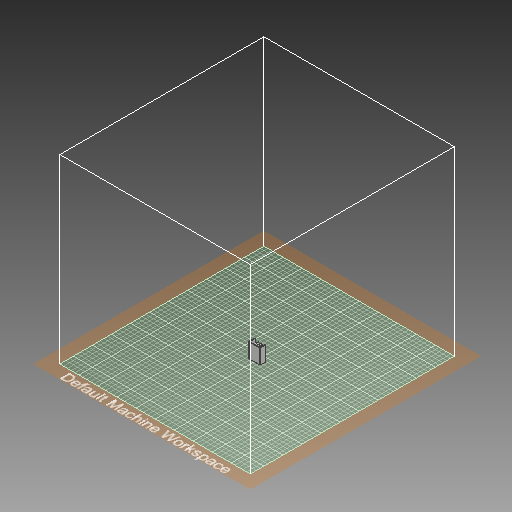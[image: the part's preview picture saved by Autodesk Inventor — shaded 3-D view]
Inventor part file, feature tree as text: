
AUTODESK INVENTOR PART (.ipt)
format: ipt  version: 2019.3 (Build 233278000, 278)  size: 1,133,056 bytes
history: native  units: mm
features: extrude x4, sketch x4, other x3, mirror x1, projected_geometry x1
ambient origin geometry x8: Origin, YZ Plane, XZ Plane, XY Plane, X Axis, Y Axis, Z Axis, Center Point
bodies: Body1 (feature_tree)
feature tree (13):
  extrude  "Extrusion2"  Depth=0.5mm
  extrude  "Extrusion4"  Depth=0.5mm
  mirror  "Mirror1"
  extrude  "Extrusion5"  Depth=0.5mm
  extrude  "Extrusion6"  Depth=1.0mm TaperAngle=360.0deg
  sketch  "Sketch5"  dims[d9=30.0deg d10=400.0mm d12=360.0deg d14=10.0mm d15=0.0mm d16=0.15mm d17=15.0mm d20=22.68928mm d21=2.0mm d22=2.0mm d23=10.0mm d24=10.0mm d25=2.0mm d26=4.0mm d27=2.0mm d28=1.0mm d29=1.0mm d30=1.0mm d31=1.0mm d32=11.0mm d34=10.0mm d35=0.0mm d36=3.0mm d37=0.0mm d38=1.0mm d39=0.0mm]
  other  "Work Point1"
  other  "Work Point2"
  sketch  "Sketch2"  dims[d3=5.047545mm d4=0.5mm]
  projected_geometry  "Projected Loop1"
  sketch  "Sketch3"  dims[d5=0.5mm d6=0.5mm]
  sketch  "Sketch4"  dims[d7=60.0deg d8=0.5mm]
  other  "Work Axis1"
